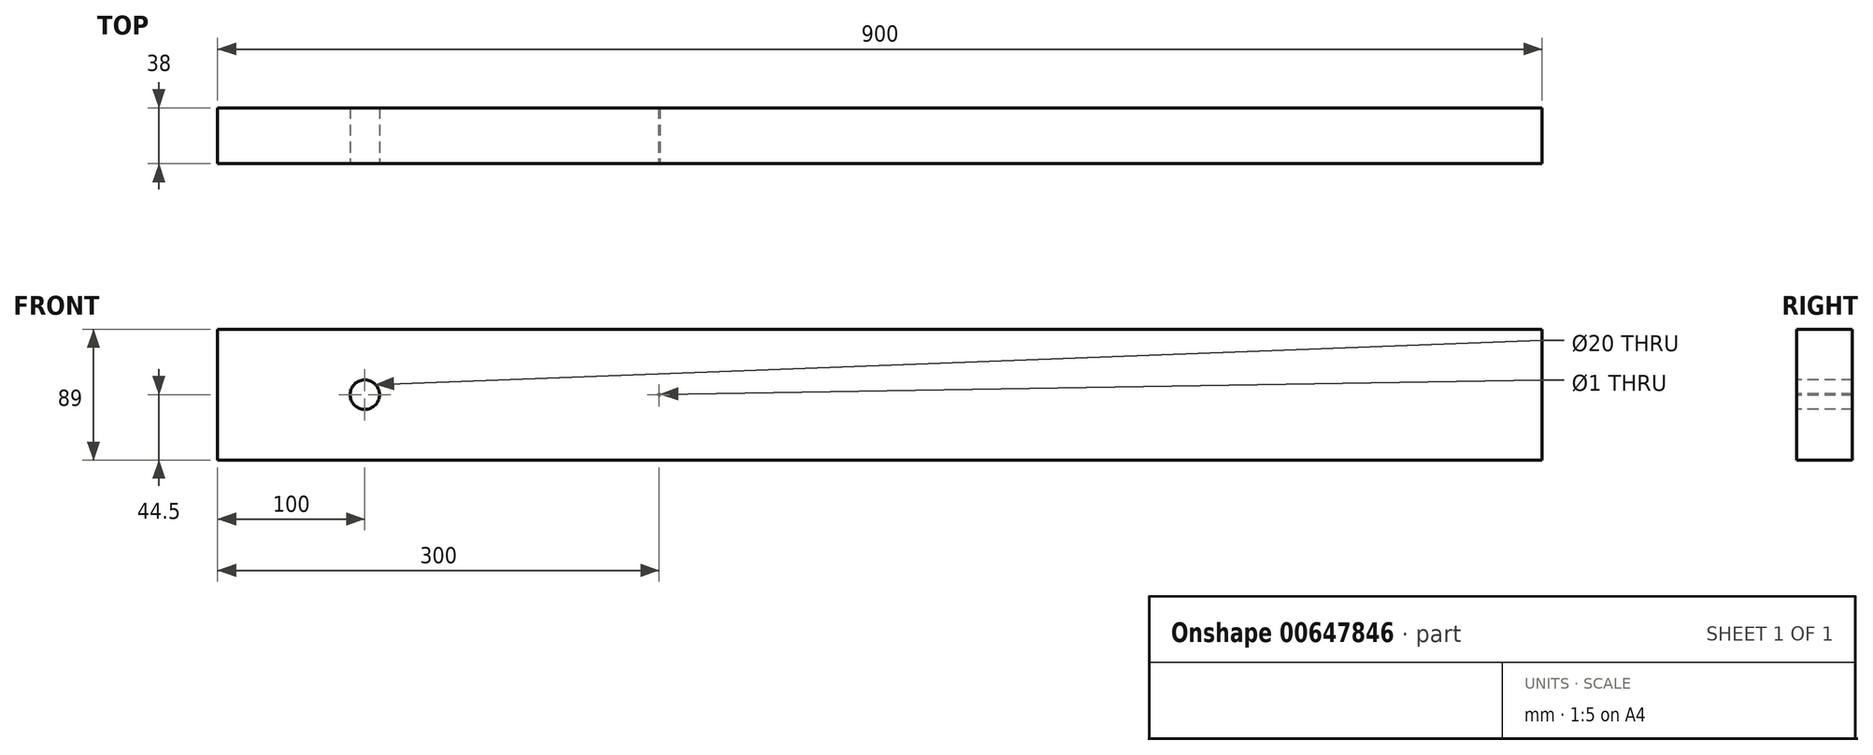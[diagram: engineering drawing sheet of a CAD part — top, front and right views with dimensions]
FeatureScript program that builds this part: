
annotation { "Feature Type Name" : "Feature", "Feature Type Description" : "" }
export const myFeature = defineFeature(function(context is Context, id is Id, definition is map)
    precondition{}
    {
        {
            var Q0;
            Q0=qCreatedBy(makeId("Front.planeOp"),FACE);
            var sketch = newSketch(context, id + "F0", { "sketchPlane" : qUnion([Q0])});
            skLineSegment(sketch, "E0.bottom", {"start": v(-450, -44.5) * mm, "end": v(450, -44.5) * mm});
            skLineSegment(sketch, "E0.top", {"start": v(-450, 44.5) * mm, "end": v(450, 44.5) * mm});
            skLineSegment(sketch, "E0.left", {"start": v(-450, -44.5) * mm, "end": v(-450, 44.5) * mm});
            skLineSegment(sketch, "E0.right", {"start": v(450, -44.5) * mm, "end": v(450, 44.5) * mm});
            skPoint(sketch, "E0.middle", {"position": v(0, 0) * mm});
            skSolve(sketch);
        }
        {
            var Q0;
            Q0=qSketchRegion(id+"F0",true);
            extrude(context, id + "F1", {"entities" : qUnion([Q0]), "depth" : 38 * mm, "offsetDistance" : 25 * mm});
        }
        {
            var Q0;
            Q0=makeQuery(id+"F1.opExtrude","CAP_FACE",FACE,{"disambiguationData":[OSD([sQuery(id+"F0.wireOp",EDGE,"E0.bottom"),sQuery(id+"F0.wireOp",EDGE,"E0.top"),sQuery(id+"F0.wireOp",EDGE,"E0.left"),sQuery(id+"F0.wireOp",EDGE,"E0.right")])],"isStart":false});
            var sketch = newSketch(context, id + "F2", { "sketchPlane" : qUnion([Q0])});
            skPoint(sketch, "E1", {"position": v(-350, 0) * mm});
            skPoint(sketch, "E2", {"position": v(-150, 0) * mm});
            skSolve(sketch);
        }
        {
            var Q0;
            Q0=sQuery(id+"F2.wireOp",VERTEX,"E1");
            var Q1;
            Q1=makeQuery(id+"F1.opExtrude","SWEPT_BODY",BODY,{"disambiguationData":[OSD([sQuery(id+"F0.wireOp",EDGE,"E0.bottom"),sQuery(id+"F0.wireOp",EDGE,"E0.top"),sQuery(id+"F0.wireOp",EDGE,"E0.left"),sQuery(id+"F0.wireOp",EDGE,"E0.right")])]});
            hole(context, id + "F3", {"style" : HoleStyle.SIMPLE, "endStyle" : HoleEndStyle.THROUGH, "holeDiameter" : 20 * mm, "majorDiameter" : 5 * mm, "isTappedThrough" : true, "tappedDepth" : 12 * mm, "tapClearance" : 3, "locations" : qUnion([Q0]), "scope" : qUnion([Q1])});
        }
        {
            var Q0;
            Q0=makeQuery(id+"F1.opExtrude","SWEPT_FACE",FACE,{"disambiguationData":[OSD([sQuery(id+"F0.wireOp",EDGE,"E0.top")])]});
            var sketch = newSketch(context, id + "F4", { "sketchPlane" : qUnion([Q0])});
            skPoint(sketch, "E3", {"position": v(-250, 0) * mm});
            skSolve(sketch);
        }
        {
            var Q0;
            Q0=sQuery(id+"F2.wireOp",VERTEX,"E2");
            var Q1;
            Q1=makeQuery(id+"F1.opExtrude","SWEPT_BODY",BODY,{"disambiguationData":[OSD([sQuery(id+"F0.wireOp",EDGE,"E0.bottom"),sQuery(id+"F0.wireOp",EDGE,"E0.top"),sQuery(id+"F0.wireOp",EDGE,"E0.left"),sQuery(id+"F0.wireOp",EDGE,"E0.right")])]});
            hole(context, id + "F5", {"style" : HoleStyle.SIMPLE, "endStyle" : HoleEndStyle.THROUGH, "holeDiameter" : 1 * mm, "majorDiameter" : 5 * mm, "isTappedThrough" : true, "tappedDepth" : 12 * mm, "tapClearance" : 3, "locations" : qUnion([Q0]), "scope" : qUnion([Q1])});
        }
    });
